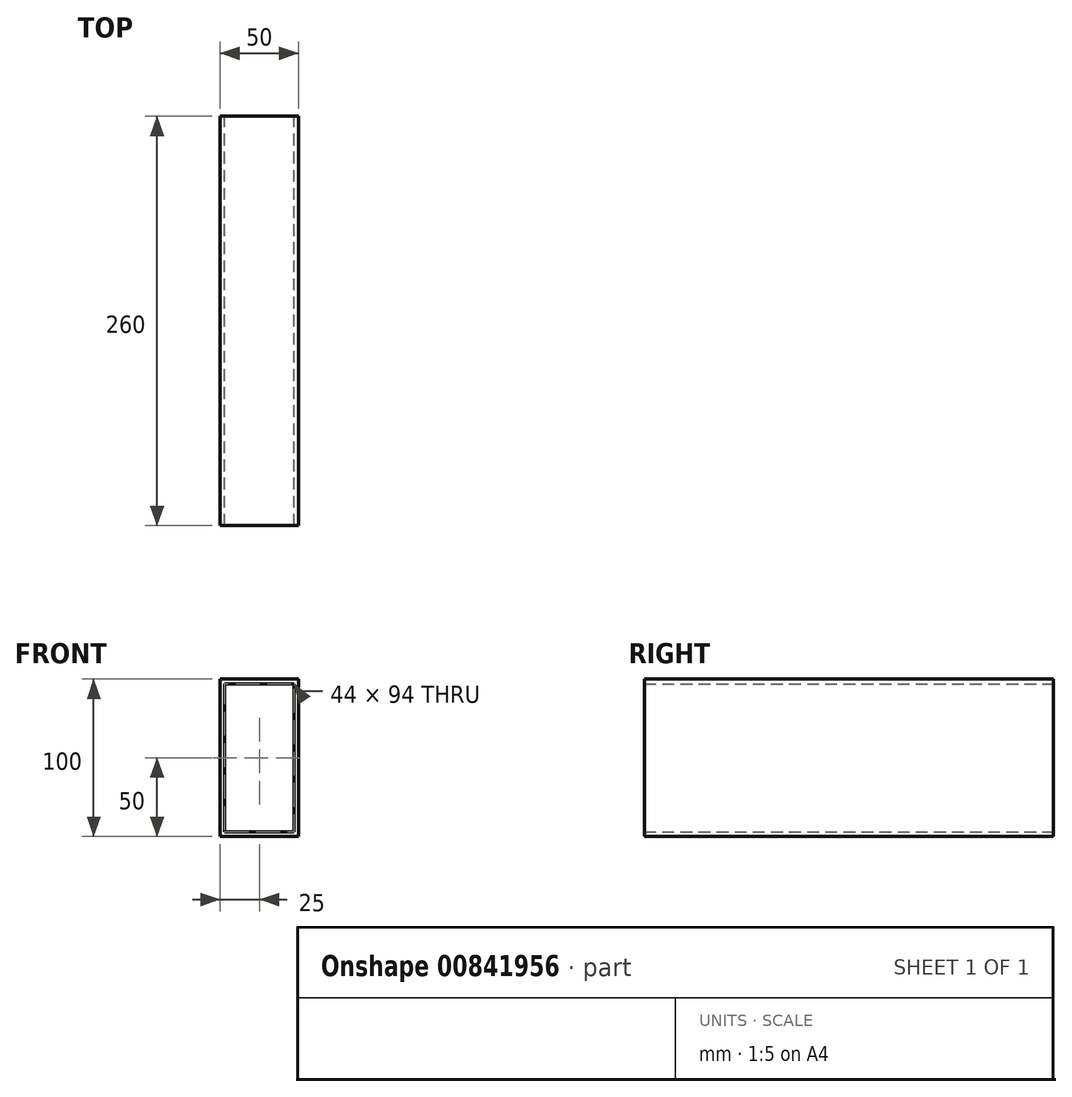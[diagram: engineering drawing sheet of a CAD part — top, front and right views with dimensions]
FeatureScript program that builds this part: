
annotation { "Feature Type Name" : "Feature", "Feature Type Description" : "" }
export const myFeature = defineFeature(function(context is Context, id is Id, definition is map)
    precondition{}
    {
        {
            var Q0;
            Q0=qCreatedBy(makeId("Front.planeOp"),FACE);
            var sketch = newSketch(context, id + "F0", { "sketchPlane" : qUnion([Q0])});
            skLineSegment(sketch, "E0.bottom", {"start": v(-25, 50) * mm, "end": v(25, 50) * mm});
            skLineSegment(sketch, "E0.top", {"start": v(-25, -50) * mm, "end": v(25, -50) * mm});
            skLineSegment(sketch, "E0.left", {"start": v(-25, 50) * mm, "end": v(-25, -50) * mm});
            skLineSegment(sketch, "E0.right", {"start": v(25, 50) * mm, "end": v(25, -50) * mm});
            skLineSegment(sketch, "E1.0", {"start": v(-22, 47) * mm, "end": v(-22, -47) * mm});
            skLineSegment(sketch, "E1.1", {"start": v(-22, 47) * mm, "end": v(22, 47) * mm});
            skLineSegment(sketch, "E1.2", {"start": v(22, 47) * mm, "end": v(22, -47) * mm});
            skLineSegment(sketch, "E1.3", {"start": v(-22, -47) * mm, "end": v(22, -47) * mm});
            skSolve(sketch);
        }
        {
            var Q0;
            Q0=makeQuery(id+"F0.imprint","IMPRINT",FACE,{"disambiguationData":[TD([[makeQuery(id+"F0.imprint","IMPRINT",EDGE,{"derivedFrom":sQuery(id+"F0.wireOp",EDGE,"E0.bottom")}),-1.0]])]});
            extrude(context, id + "F1", {"entities" : qUnion([Q0]), "endBound" : BoundingType.SYMMETRIC, "depth" : 260 * mm, "offsetDistance" : 25 * mm});
        }
    });
